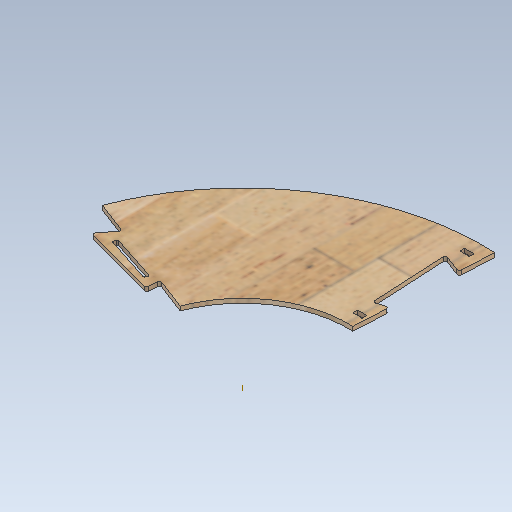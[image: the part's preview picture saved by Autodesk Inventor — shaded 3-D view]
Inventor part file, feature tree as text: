
AUTODESK INVENTOR PART (.ipt)
format: ipt  version: 2020 (Build 240168000, 168)  size: 460,288 bytes
history: native  units: mm
features: extrude x5, sketch x4, pattern_circular x3, mirror x1
ambient origin geometry x8: Origin, YZ Plane, XZ Plane, XY Plane, X Axis, Y Axis, Z Axis, Center Point
bodies: Body1 (feature_tree)
feature tree (13):
  extrude  "Extrusion3"  Depth=6.5mm
  extrude  "Extrusion4"  Depth=2.666667mm
  extrude  "Extrusion5"  Depth=1.333333mm
  sketch  "Sketch5"  dims[d32=1.333333mm d33=1.333333mm]
  extrude  "Extrusion7"  Depth=145.0mm
  pattern_circular  "Circular Pattern2"  Angle=90.0deg  [1 undecoded]
  pattern_circular  "Circular Pattern3"  [2 undecoded]
  mirror  "Mirror3"
  pattern_circular  "Circular Pattern4"  Angle=90.0deg  [1 undecoded]
  extrude  "Extrusion10"  Depth=145.0mm
  sketch  "Sketch2"  dims[d15=6.0mm d16=0.0mm d21=6.5mm]
  sketch  "Sketch3"  dims[d24=2.666667mm d25=2.666667mm]
  sketch  "Sketch6"  dims[d38=0.0mm d39=0.0mm d40=3.25mm d41=90.0deg d42=3.25mm d43=90.0deg d52=4.363323mm d54=10.0mm d55=0.0mm d60=0.872665mm d61=12.566371mm d62=13.439035mm d63=2.666667mm d64=0.523599mm d66=0.523599mm d67=2.666667mm d68=2.666667mm d70=12.566371mm d71=12.566371mm d84=300.14mm d85=682.72mm d86=491.43mm d87=150.07mm d88=341.36mm d89=4.363323mm d90=1.919862mm d91=1.919862mm d94=300.14mm d95=682.72mm d104=6.5mm d105=12.0mm d108=1.333333mm d109=1.333333mm d110=1.333333mm d111=1.333333mm d112=0.0mm d113=0.0mm d114=0.0mm d145=20.0mm d146=12.566371mm d149=145.0mm d150=90.0deg d151=90.0deg d152=90.0deg d153=90.0deg d154=20.0mm d155=25.132741mm d157=20.0mm d158=25.132741mm d169=0.0mm d170=0.0mm]
note: 4 required parameter values undecoded (feature->parameter linkage not recoverable at this tier; creation-order binding heuristic only, values carry confidence <= 0.55)
